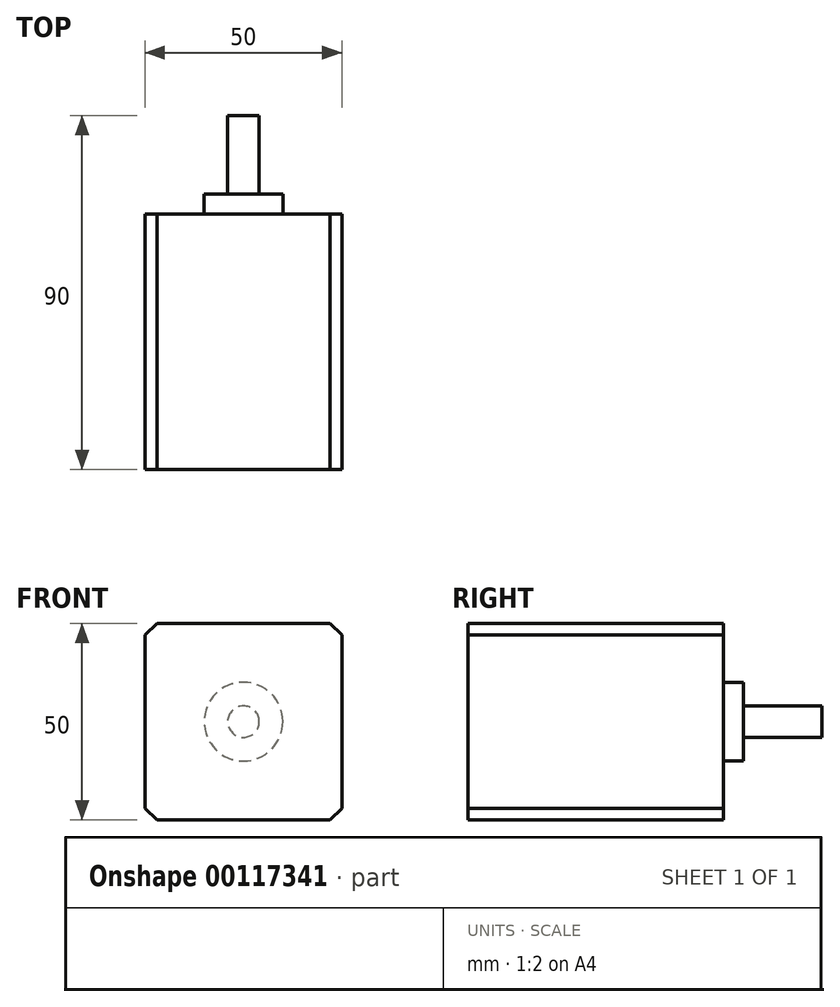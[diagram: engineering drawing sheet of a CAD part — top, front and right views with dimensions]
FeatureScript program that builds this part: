
annotation { "Feature Type Name" : "Feature", "Feature Type Description" : "" }
export const myFeature = defineFeature(function(context is Context, id is Id, definition is map)
    precondition{}
    {
        {
            var Q0;
            Q0=qCreatedBy(makeId("Front.planeOp"),FACE);
            var sketch = newSketch(context, id + "F0", { "sketchPlane" : qUnion([Q0])});
            skLineSegment(sketch, "E0.bottom", {"start": v(25, -25) * mm, "end": v(-25, -25) * mm});
            skLineSegment(sketch, "E0.top", {"start": v(25, 25) * mm, "end": v(-25, 25) * mm});
            skLineSegment(sketch, "E0.left", {"start": v(25, -25) * mm, "end": v(25, 25) * mm});
            skLineSegment(sketch, "E0.right", {"start": v(-25, -25) * mm, "end": v(-25, 25) * mm});
            skPoint(sketch, "E0.middle", {"position": v(0, 0) * mm});
            skSolve(sketch);
        }
        {
            var Q0;
            Q0 = qSketchRegion(id + "F0", true);
            extrude(context, id + "F1", {"entities" : qUnion([Q0]), "depth" : 65 * mm});
        }
        {
            var Q0;
            Q0=makeQuery(id+"F1.opExtrude","CAP_FACE",FACE,{"disambiguationData":[OSD([sQuery(id+"F0.wireOp",EDGE,"E0.bottom"),sQuery(id+"F0.wireOp",EDGE,"E0.top"),sQuery(id+"F0.wireOp",EDGE,"E0.left"),sQuery(id+"F0.wireOp",EDGE,"E0.right")])],"isStart":true});
            var sketch = newSketch(context, id + "F2", { "sketchPlane" : qUnion([Q0])});
            skCircle(sketch, "E1", {"center": v(0, 0) * mm, "radius": 10 * mm});
            skSolve(sketch);
        }
        {
            var Q0;
            Q0 = qSketchRegion(id + "F2", true);
            extrude(context, id + "F3", {"entities" : qUnion([Q0]), "operationType" : NewBodyOperationType.ADD, "depth" : 5 * mm});
        }
        {
            var Q0;
            Q0=makeQuery(id+"F3.opExtrude","CAP_FACE",FACE,{"disambiguationData":[OSD([sQuery(id+"F2.wireOp",EDGE,"E1")])],"isStart":false});
            var sketch = newSketch(context, id + "F4", { "sketchPlane" : qUnion([Q0])});
            skCircle(sketch, "E2", {"center": v(0, 0) * mm, "radius": 4 * mm});
            skSolve(sketch);
        }
        {
            var Q0;
            Q0 = qSketchRegion(id + "F4", true);
            extrude(context, id + "F5", {"entities" : qUnion([Q0]), "operationType" : NewBodyOperationType.ADD, "depth" : 20 * mm});
        }
        {
            var Q0;
            Q0=makeQuery(id+"F1.opExtrude","SWEPT_EDGE",EDGE,{"disambiguationData":[OSD([sQuery(id+"F0.wireOp",EDGE,"E0.top"),sQuery(id+"F0.wireOp",EDGE,"E0.right")])]});
            var Q1;
            Q1=makeQuery(id+"F1.opExtrude","SWEPT_EDGE",EDGE,{"disambiguationData":[OSD([sQuery(id+"F0.wireOp",EDGE,"E0.bottom"),sQuery(id+"F0.wireOp",EDGE,"E0.right")])]});
            var Q2;
            Q2=makeQuery(id+"F1.opExtrude","SWEPT_EDGE",EDGE,{"disambiguationData":[OSD([sQuery(id+"F0.wireOp",EDGE,"E0.bottom"),sQuery(id+"F0.wireOp",EDGE,"E0.left")])]});
            var Q3;
            Q3=makeQuery(id+"F1.opExtrude","SWEPT_EDGE",EDGE,{"disambiguationData":[OSD([sQuery(id+"F0.wireOp",EDGE,"E0.top"),sQuery(id+"F0.wireOp",EDGE,"E0.left")])]});
            chamfer(context, id + "F6", {"entities" : qUnion([Q0, Q1, Q2, Q3]), "width" : 3 * mm, "tangentPropagation" : true});
        }
    });
